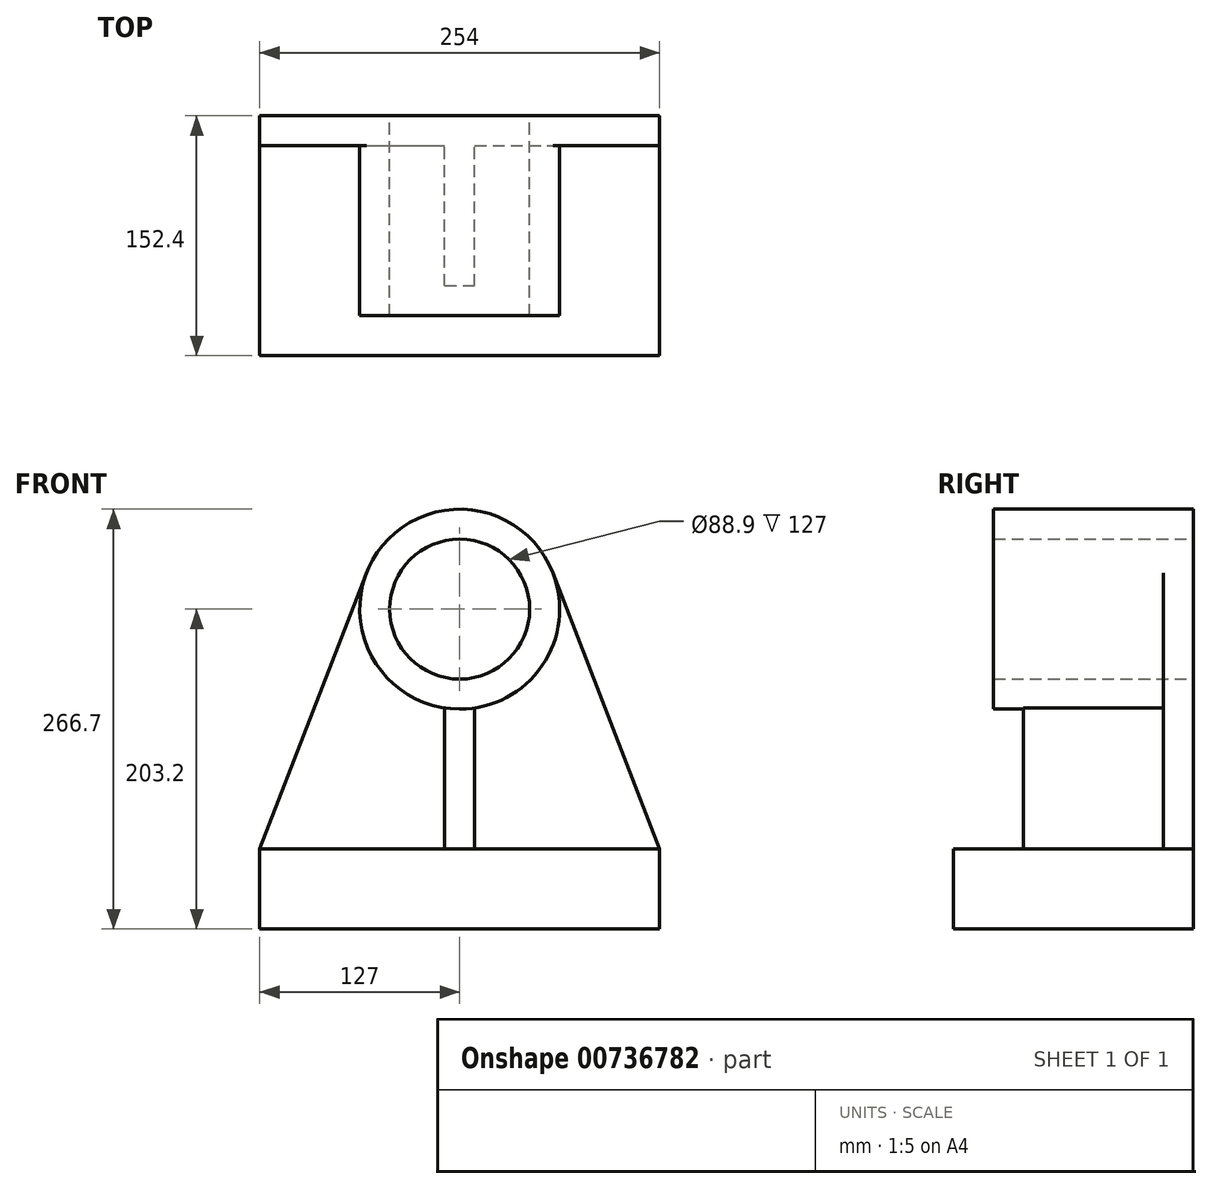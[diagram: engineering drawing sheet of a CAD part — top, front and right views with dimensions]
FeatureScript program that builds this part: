
annotation { "Feature Type Name" : "Feature", "Feature Type Description" : "" }
export const myFeature = defineFeature(function(context is Context, id is Id, definition is map)
    precondition{}
    {
        {
            var Q0;
            Q0=qCreatedBy(makeId("Front.planeOp"),FACE);
            var sketch = newSketch(context, id + "F0", { "sketchPlane" : qUnion([Q0])});
            skCircle(sketch, "E0", {"center": v(0, 0) * mm, "radius": 44.45 * mm});
            skCircle(sketch, "E1", {"center": v(0, 0) * mm, "radius": 63.5 * mm});
            skSolve(sketch);
        }
        {
            var Q0;
            Q0 = qSketchRegion(id + "F0", true);
            extrude(context, id + "F1", {"entities" : qUnion([Q0]), "depth" : 127 * mm, "offsetDistance" : 25.4 * mm});
        }
        {
            var Q0;
            Q0=qCreatedBy(makeId("Front.planeOp"),FACE);
            var sketch = newSketch(context, id + "F2", { "sketchPlane" : qUnion([Q0])});
            skArc(sketch, "E2.0", {"start": v(-59.23, 22.9) * mm, "mid": v(0, -63.5) * mm, "end": v(59.23, 22.9) * mm});
            skLineSegment(sketch, "E3", {"start": v(-59.23, 22.9) * mm, "end": v(-127, -152.4) * mm});
            skLineSegment(sketch, "E4", {"start": v(-127, -152.4) * mm, "end": v(127, -152.4) * mm});
            skLineSegment(sketch, "E5", {"start": v(127, -152.4) * mm, "end": v(59.23, 22.9) * mm});
            skSolve(sketch);
        }
        {
            var Q0;
            Q0=makeQuery(id+"F2.imprint","IMPRINT",FACE,{"disambiguationData":[TD([[makeQuery(id+"F2.imprint","IMPRINT",EDGE,{"derivedFrom":sQuery(id+"F2.wireOp",EDGE,"E2.0")}),-1.0]])]});
            extrude(context, id + "F3", {"entities" : qUnion([Q0]), "operationType" : NewBodyOperationType.ADD, "depth" : 19.05 * mm, "offsetDistance" : 25.4 * mm});
        }
        {
            var Q0;
            Q0=qCreatedBy(makeId("Front.planeOp"),FACE);
            var sketch = newSketch(context, id + "F4", { "sketchPlane" : qUnion([Q0])});
            skLineSegment(sketch, "E6.0", {"start": v(-127, -152.4) * mm, "end": v(127, -152.4) * mm});
            skLineSegment(sketch, "E7", {"start": v(-127, -152.4) * mm, "end": v(-127, -203.2) * mm});
            skLineSegment(sketch, "E8", {"start": v(-127, -203.2) * mm, "end": v(127, -203.2) * mm});
            skLineSegment(sketch, "E9", {"start": v(127, -203.2) * mm, "end": v(127, -152.4) * mm});
            skSolve(sketch);
        }
        {
            var Q0;
            Q0 = qSketchRegion(id + "F4", true);
            extrude(context, id + "F5", {"entities" : qUnion([Q0]), "operationType" : NewBodyOperationType.ADD, "depth" : 152.4 * mm, "offsetDistance" : 25.4 * mm});
        }
        {
            var Q0;
            Q0=makeQuery(id+"F3.opExtrude","CAP_FACE",FACE,{"disambiguationData":[OSD([sQuery(id+"F2.wireOp",EDGE,"E2.0"),sQuery(id+"F2.wireOp",EDGE,"E3"),sQuery(id+"F2.wireOp",EDGE,"E4"),sQuery(id+"F2.wireOp",EDGE,"E5")])],"isStart":false});
            var sketch = newSketch(context, id + "F6", { "sketchPlane" : qUnion([Q0])});
            skArc(sketch, "E10.0", {"start": v(-9.53, -62.78) * mm, "mid": v(0, -63.5) * mm, "end": v(9.53, -62.78) * mm});
            skLineSegment(sketch, "E11.0", {"start": v(-9.52, -152.4) * mm, "end": v(9.53, -152.4) * mm});
            skLineSegment(sketch, "E12", {"start": v(-9.52, -62.78) * mm, "end": v(-9.52, -152.4) * mm});
            skLineSegment(sketch, "E13", {"start": v(9.53, -62.78) * mm, "end": v(9.53, -152.4) * mm});
            skPoint(sketch, "E14.orphan", {"position": v(-127, -152.4) * mm});
            skPoint(sketch, "E15.orphan", {"position": v(127, -152.4) * mm});
            skSolve(sketch);
        }
        {
            var Q0;
            Q0 = qSketchRegion(id + "F6", true);
            extrude(context, id + "F7", {"entities" : qUnion([Q0]), "operationType" : NewBodyOperationType.ADD, "depth" : 88.9 * mm, "offsetDistance" : 25.4 * mm});
        }
    });
